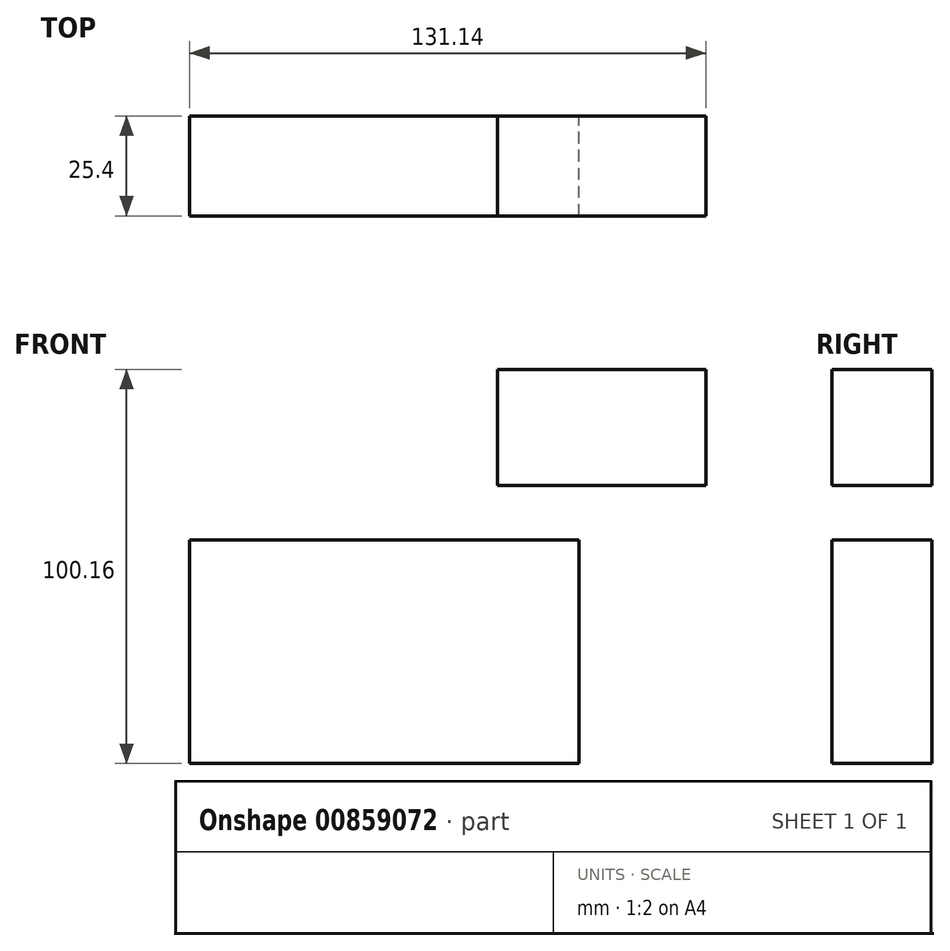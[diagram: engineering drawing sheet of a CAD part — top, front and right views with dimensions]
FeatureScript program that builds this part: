
annotation { "Feature Type Name" : "Feature", "Feature Type Description" : "" }
export const myFeature = defineFeature(function(context is Context, id is Id, definition is map)
    precondition{}
    {
        {
            var Q0;
            Q0=qCreatedBy(makeId("Front.planeOp"),FACE);
            var sketch = newSketch(context, id + "F0", { "sketchPlane" : qUnion([Q0])});
            skLineSegment(sketch, "E0.bottom", {"start": v(-49.48, 28.42) * mm, "end": v(49.48, 28.42) * mm});
            skLineSegment(sketch, "E0.top", {"start": v(-49.48, -28.42) * mm, "end": v(49.48, -28.42) * mm});
            skLineSegment(sketch, "E0.left", {"start": v(-49.48, 28.42) * mm, "end": v(-49.48, -28.42) * mm});
            skLineSegment(sketch, "E0.right", {"start": v(49.48, 28.42) * mm, "end": v(49.48, -28.42) * mm});
            skPoint(sketch, "E0.middle", {"position": v(0, 0) * mm});
            skSolve(sketch);
        }
        {
            var Q0;
            Q0=qCreatedBy(makeId("Front.planeOp"),FACE);
            var sketch = newSketch(context, id + "F1", { "sketchPlane" : qUnion([Q0])});
            skLineSegment(sketch, "E1.bottom", {"start": v(81.66, 71.74) * mm, "end": v(28.73, 71.74) * mm});
            skLineSegment(sketch, "E1.top", {"start": v(81.66, 42.26) * mm, "end": v(28.73, 42.26) * mm});
            skLineSegment(sketch, "E1.left", {"start": v(81.66, 71.74) * mm, "end": v(81.66, 42.26) * mm});
            skLineSegment(sketch, "E1.right", {"start": v(28.73, 71.74) * mm, "end": v(28.73, 42.26) * mm});
            skPoint(sketch, "E1.middle", {"position": v(55.2, 57) * mm});
            skSolve(sketch);
        }
        {
            var Q0;
            Q0=makeQuery(id+"F0.imprint","IMPRINT",FACE,{"disambiguationData":[TD([[makeQuery(id+"F0.imprint","IMPRINT",EDGE,{"derivedFrom":sQuery(id+"F0.wireOp",EDGE,"E0.bottom")}),-1.0]])]});
            var sketch = newSketch(context, id + "F2", { "sketchPlane" : qUnion([Q0])});
            skLineSegment(sketch, "E2", {"start": v(49.78, 28.12) * mm, "end": v(49.78, 36.25) * mm});
            skArc(sketch, "E3", {"start": v(49.78, 36.25) * mm, "mid": v(53, 43.7) * mm, "end": v(60.6, 46.47) * mm});
            skSolve(sketch);
        }
        {
            var Q0;
            Q0=makeQuery(id+"F2.imprint","IMPRINT",FACE,{"disambiguationData":[TD([[makeQuery(id+"F2.imprint","IMPRINT",EDGE,{"derivedFrom":makeQuery(id+"F0.imprint","IMPRINT",EDGE,{"derivedFrom":sQuery(id+"F0.wireOp",EDGE,"E0.bottom")})}),-1.0]])]});
            var Q1;
            Q1=makeQuery(id+"F1.imprint","IMPRINT",FACE,{"disambiguationData":[TD([[makeQuery(id+"F1.imprint","IMPRINT",EDGE,{"derivedFrom":sQuery(id+"F1.wireOp",EDGE,"E1.bottom")}),1.0]])]});
            extrude(context, id + "F3", {"entities" : qUnion([Q0, Q1]), "depth" : 25.4 * mm, "offsetDistance" : 25.4 * mm});
        }
    });
